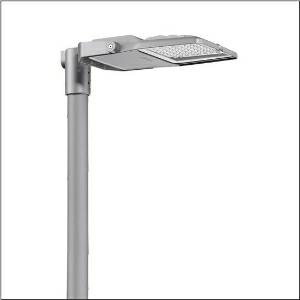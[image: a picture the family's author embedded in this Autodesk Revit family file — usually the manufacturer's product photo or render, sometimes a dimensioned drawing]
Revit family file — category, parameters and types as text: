
# Revit family: floodlight_fl_21_mini___pl52_5xa7776d2d3a_85e1
name_source: partatom
category: Lighting Fixtures
units: mm (PartAtom-declared; Revit-internal decimal feet)

## family parameters
Cut with Voids When Loaded = No
Host = Face
Light Source = No
Part Type = Normal
Room Calculation Point = No
Round Connector Dimension = Use Diameter
Shared = No

## types (1)
- --- (1 x LED, 17840 lm, 142.9 W, 3000K)
    Apparent Load = 143 VA
    CIE Flux Codes = 26 60 98 100 100
    Color Rendering = 70
    Color Temperature = 3000K
    Default Elevation = 1800 mm
    Description = Floodlight FL 21 mini, floodlight, primary light control with lens, of PMMA, primary optical cover: protective disc, of toughened safety glass, transparent, light distribution: PL52, light emission: direct distribution, installation type: surface-mounted, LED, High Power LED, rated luminous flux: 17.840lm, luminous efficacy: 125lm/W, light colour: 730, colour temperature: 3000K, control gear: Smart Interface (Zhaga), control: flexible luminous flux parameterisation, time-dependent luminous flux control, constant luminous flux control, overheat protection, pre-setting: logarithmic dimming characteristic, with terminal, 6-pole, mains connection: 220..240V, AC, 50/60Hz, start of lifetime: 143W, end of service life: 151W, reduction: 63W, luminaire housing, of diecast aluminium, powder-coated, Siteco® metallic grey (DB 702S), corrosivity category C5 mid according to DIN EN ISO 12944, suitable for swimming pools, chlorine-resistant, sealing non-destructively replaceable, please order mast flange separately, mast bracket, of steel, galvanised, powder-coated, Siteco® metallic grey (DB 702S), Smart Interface below and above, protection rating (complete): IP66, insulation class (complete): insulation class II (safety insulation), certification: CE, ENEC, VDE, protection symbol: D, impact resistance: IK08, permissible operating ambient temperature: -40..+40°C, permissible operating ambient temperature for outdoor applications: -40..+50°C, standard: DIN EN 12944, LABS conformity tested according to VDMA 24364:2018-05, packaging unit: 1 piece

Light Distribution: PL52
    Height = 70 mm
    Lamp = 1 x LED
    Lamp Light Flux = 17840 lm
    Lamp Power = 142.9 W
    Lamp count = 1
    Length = 485 mm
    Luminous efficacy = 125 lm/W
    Manufacturer = Siteco
    ModVariant = No
    Model = 5XA7776D2D3A
    Number of Poles = 1
    OnlyDefault = Yes
    Power Factor = 1
    Product Name = Floodlight FL 21 mini | PL52
    Product group = floodlight | pylon annexe
    ProductGroupID = 6200
    Protection Class = Protection class II
    Protection Degree = IP 66
    RLX_Detail_Level = 1
    RLX_Emergency_Light_Flux = 0 lm
    RLX_Emergency_Type = 0
    RLX_Emergency_Type_DB = No
    RlxData = <blob elided: 101601 chars, md5=b5152221>
    Socket = socket
    Standby Power = 0 W
    System Light Flux = 17840 lm
    System Power = 143 W
    Type Comments = factory setting: luminous flux: 100 % | dim-lin: 254 | 730 mA
    Type Image = l_1007125.jpg
    URL = http://relux.com
    VarID = @adj_163114
    Voltage = 0 V
    Weight = 0.00 kg
    Width = 337 mm

## geometry (parser evidence)
native form markers: Blend x4, Sweep x11
no freeform markers — native parametric forms only
